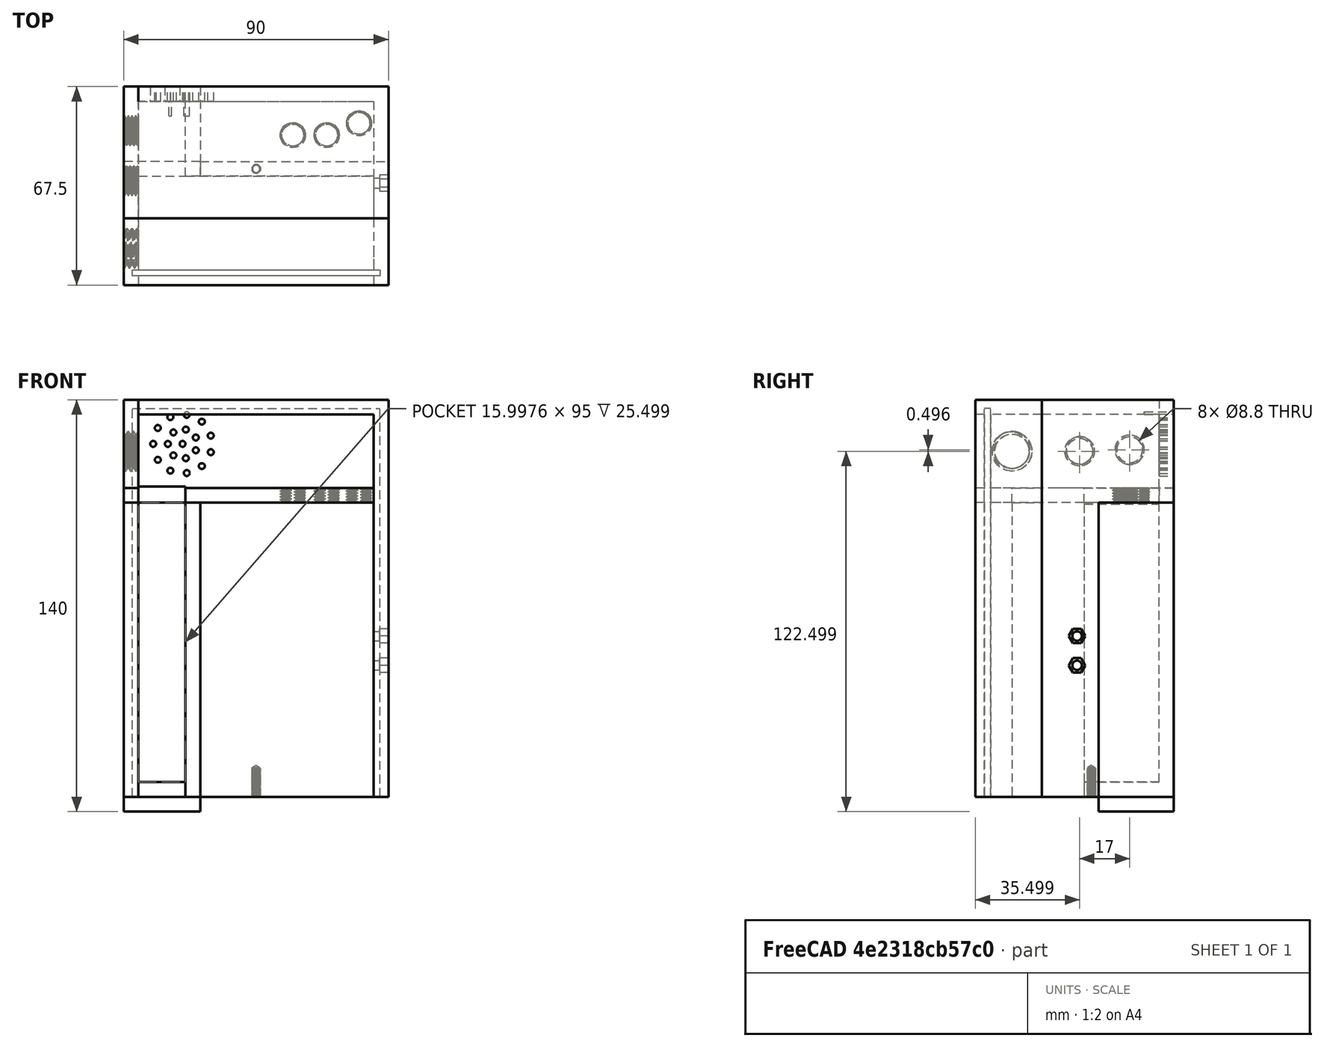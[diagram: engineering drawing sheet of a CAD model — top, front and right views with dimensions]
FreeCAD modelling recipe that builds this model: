
FCSTD DOCUMENT  (FreeCAD 1.0R39285 (Git))
Label: QMX_batterycase7b
License: All rights reserved
LicenseURL: https://en.wikipedia.org/wiki/All_rights_reserved
objects: Sketcher::SketchObject×24, PartDesign::Pad×22, PartDesign::Pocket×10, PartDesign::Hole×5, Part::FeaturePython×3, PartDesign::PolarPattern×2, PartDesign::Body×2, Part::Extrusion×2, App::DocumentObjectGroup×1, PartDesign::FeatureBase×1
note: 172 computed .brp shape members not serialized (recipe doc carries the construction recipe); baked Part::Feature solids carry a one-line shape summary decoded from their .brp

FEATURE [Sketcher::SketchObject] Sketch
  ArcFitTolerance = 1e-06
  FullyConstrained = true
  MakeInternals = false
  sketch-geometry (7):
    g0: LineSegment StartX=0 StartY=0 StartZ=0 EndX=0 EndY=25 EndZ=0
    g1: LineSegment StartX=0 StartY=25 StartZ=0 EndX=-45 EndY=25 EndZ=0
    g2: LineSegment StartX=-45 StartY=25 StartZ=0 EndX=-45 EndY=0 EndZ=0
    g3: LineSegment StartX=-45 StartY=0 StartZ=0 EndX=0 EndY=0 EndZ=0
    g4: Circle CenterX=-32.5 CenterY=8.5 CenterZ=0 NormalX=0 NormalY=0 NormalZ=1 AngleXU=0 Radius=3.65
    g5: Circle CenterX=-21 CenterY=8.5 CenterZ=0 NormalX=0 NormalY=0 NormalZ=1 AngleXU=0 Radius=3.7
    g6: Circle CenterX=-10 CenterY=12.5 CenterZ=0 NormalX=0 NormalY=0 NormalZ=1 AngleXU=0 Radius=3.75
  constraints (20):
    c: Coincident(g0,g1)
    c: Coincident(g1,g2)
    c: Coincident(g2,g3)
    c: Coincident(g3,g0)
    c: Vertical(g0)
    c: Vertical(g2)
    c: Horizontal(g1)
    c: Horizontal(g3)
    c: Distance(g0,g2) = 45
    c: Distance(g1,g3) = 25
    c: Coincident(g0,g-1)
    c: Diameter(g4) = 7.3
    c: Diameter(g5) = 7.4
    c: Diameter(g6) = 7.5
    c: DistanceX(g4) = -32.5
    c: DistanceY(g4) = 8.5
    c: DistanceX(g5) = -21
    c: DistanceY(g5) = 8.5
    c: DistanceX(g6) = -10
    c: DistanceY(g6) = 12.5
FEATURE [PartDesign::Pad] Pad
  Direction = (0,0,1)
  Length = 5
  Length2 = 10
  Profile = -> Sketch
  ReferenceAxis = -> Sketch [N_Axis]
  Refine = true
  Suppressed = false
  Type = 0
FEATURE [PartDesign::Hole] Hole
  BaseFeature = -> Pad
  CustomThreadClearance = 1.5
  Depth = 25
  DepthType = 0
  Diameter = 7.5
  DrillForDepth = false
  DrillPoint = 1
  DrillPointAngle = 118
  HoleCutCountersinkAngle = 90
  HoleCutCustomValues = false
  HoleCutDepth = 0
  HoleCutDiameter = 7.1
  HoleCutType = 0
  ModelThread = true
  Profile = -> Pad [Edge21,Edge18,Edge15]
  Refine = true
  Suppressed = false
  Tapered = false
  TaperedAngle = 90
  ThreadClass = 0
  ThreadDepth = 25
  ThreadDepthType = 0
  ThreadDirection = 0
  ThreadFit = 0
  ThreadSize = 15
  ThreadType = 1
  Threaded = true
  UseCustomThreadClearance = true
FEATURE [PartDesign::Pad] Pad001
  BaseFeature = -> Hole
  Direction = (-1,0,0)
  Length = 18
  Length2 = 10
  Profile = -> Hole [Face6]
  Refine = true
  Suppressed = false
  Type = 0
FEATURE [PartDesign::Pad] Pad002
  BaseFeature = -> Pad001
  Direction = (0,-1,0)
  Length = 25
  Length2 = 10
  Profile = -> Pad001 [Face2]
  Refine = true
  Suppressed = false
  Type = 0
FEATURE [Sketcher::SketchObject] Sketch001
  ArcFitTolerance = 1e-06
  AttachmentSupport = -> [Pad002]
  FullyConstrained = true
  MakeInternals = false
  MapMode = 5
  Placement = pos=(0,0,5) rot=(0,0,1;0rad)
FEATURE [PartDesign::Pad] Pad003
  BaseFeature = -> Pad002
  Direction = (-1,0,0)
  Length = 27
  Length2 = 10
  Profile = -> Pad002 [Face75]
  Refine = true
  Suppressed = false
  Type = 0
FEATURE [Sketcher::SketchObject] Sketch002
  ArcFitTolerance = 1e-06
  AttachmentSupport = -> [Pad003]
  FullyConstrained = false
  MakeInternals = false
  MapMode = 5
  Placement = pos=(0,0,5) rot=(0,0,1;0rad)
  sketch-geometry (4):
    g0: LineSegment StartX=-5 StartY=25 StartZ=0 EndX=-5 EndY=-25 EndZ=0
    g1: LineSegment StartX=-5 StartY=-25 StartZ=0 EndX=0 EndY=-25 EndZ=0
    g2: LineSegment StartX=0 StartY=-25 StartZ=0 EndX=0 EndY=25 EndZ=0
    g3: LineSegment StartX=0 StartY=25 StartZ=0 EndX=-5 EndY=25 EndZ=0
  constraints (11):
    c: Coincident(g0,g1)
    c: Coincident(g1,g2)
    c: Coincident(g2,g3)
    c: Coincident(g3,g0)
    c: Vertical(g0)
    c: Vertical(g2)
    c: Horizontal(g1)
    c: Horizontal(g3)
    c: Distance(g0,g2) = 5
    c: Distance(g1,g3) = 50
    c: PointOnObject(g1,g-2)
FEATURE [PartDesign::Pad] Pad004
  BaseFeature = -> Pad003
  Direction = (0,0,1)
  Length = 30
  Length2 = 10
  Profile = -> Sketch002
  ReferenceAxis = -> Sketch002 [N_Axis]
  Refine = true
  Suppressed = false
  Type = 0
FEATURE [Sketcher::SketchObject] Sketch003
  ArcFitTolerance = 1e-06
  AttachmentSupport = -> [Pad004]
  FullyConstrained = false
  MakeInternals = false
  MapMode = 5
  Placement = pos=(0,0,5) rot=(0,0,1;0rad)
  sketch-geometry (4):
    g0: LineSegment StartX=-90 StartY=25.0006 StartZ=0 EndX=-90 EndY=-24.9994 EndZ=0
    g1: LineSegment StartX=-90 StartY=-24.9994 StartZ=0 EndX=-85 EndY=-24.9994 EndZ=0
    g2: LineSegment StartX=-85 StartY=-24.9994 StartZ=0 EndX=-85 EndY=25.0006 EndZ=0
    g3: LineSegment StartX=-85 StartY=25.0006 StartZ=0 EndX=-90 EndY=25.0006 EndZ=0
  constraints (10):
    c: Coincident(g0,g1)
    c: Coincident(g1,g2)
    c: Coincident(g2,g3)
    c: Coincident(g3,g0)
    c: Vertical(g0)
    c: Vertical(g2)
    c: Horizontal(g1)
    c: Horizontal(g3)
    c: Distance(g0,g2) = 5
    c: Distance(g1,g3) = 50
FEATURE [PartDesign::Pad] Pad005
  BaseFeature = -> Pad004
  Direction = (0,0,1)
  Length = 30
  Length2 = 10
  Profile = -> Sketch003
  ReferenceAxis = -> Sketch003 [N_Axis]
  Refine = true
  Suppressed = false
  Type = 0
FEATURE [Sketcher::SketchObject] Sketch004
  ArcFitTolerance = 1e-06
  AttachmentSupport = -> [Pad005]
  FullyConstrained = false
  MakeInternals = false
  MapMode = 5
  Placement = pos=(0,0,5) rot=(0,0,1;0rad)
  sketch-geometry (4):
    g0: LineSegment StartX=-84.9972 StartY=24.9988 StartZ=0 EndX=-84.9972 EndY=19.9988 EndZ=0
    g1: LineSegment StartX=-84.9972 StartY=19.9988 StartZ=0 EndX=-4.99721 EndY=19.9988 EndZ=0
    g2: LineSegment StartX=-4.99721 StartY=19.9988 StartZ=0 EndX=-4.99721 EndY=24.9988 EndZ=0
    g3: LineSegment StartX=-4.99721 StartY=24.9988 StartZ=0 EndX=-84.9972 EndY=24.9988 EndZ=0
  constraints (10):
    c: Coincident(g0,g1)
    c: Coincident(g1,g2)
    c: Coincident(g2,g3)
    c: Coincident(g3,g0)
    c: Vertical(g0)
    c: Vertical(g2)
    c: Horizontal(g1)
    c: Horizontal(g3)
    c: Distance(g0,g2) = 80
    c: Distance(g1,g3) = 5
FEATURE [PartDesign::Pad] Pad006
  BaseFeature = -> Pad005
  Direction = (0,0,1)
  Length = 30
  Length2 = 10
  Profile = -> Sketch004
  ReferenceAxis = -> Sketch004 [N_Axis]
  Refine = true
  Suppressed = false
  Type = 0
FEATURE [Sketcher::SketchObject] Sketch005
  ArcFitTolerance = 1e-06
  AttachmentSupport = -> [Pad006]
  FullyConstrained = false
  MakeInternals = false
  MapMode = 5
  Placement = pos=(-5,0,0) rot=(0.57735,-0.57735,-0.57735;2.0944rad)
  sketch-geometry (4):
    g0: LineSegment StartX=-20 StartY=35 StartZ=0 EndX=-20 EndY=30 EndZ=0
    g1: LineSegment StartX=-20 StartY=30 StartZ=0 EndX=25 EndY=30 EndZ=0
    g2: LineSegment StartX=25 StartY=30 StartZ=0 EndX=25 EndY=35 EndZ=0
    g3: LineSegment StartX=25 StartY=35 StartZ=0 EndX=-20 EndY=35 EndZ=0
  constraints (10):
    c: Coincident(g0,g1)
    c: Coincident(g1,g2)
    c: Coincident(g2,g3)
    c: Coincident(g3,g0)
    c: Vertical(g0)
    c: Vertical(g2)
    c: Horizontal(g1)
    c: Horizontal(g3)
    c: Distance(g0,g2) = 45
    c: Distance(g1,g3) = 5
FEATURE [PartDesign::Pad] Pad007
  BaseFeature = -> Pad006
  Direction = (-1,0,0)
  Length = 80
  Length2 = 10
  Profile = -> Sketch005
  ReferenceAxis = -> Sketch005 [N_Axis]
  Refine = true
  Suppressed = false
  Type = 0
FEATURE [Sketcher::SketchObject] Sketch006
  ArcFitTolerance = 1e-06
  AttachmentSupport = -> [Pad007]
  FullyConstrained = false
  MakeInternals = false
  MapMode = 5
  Placement = pos=(0,0,0) rot=(1,0,0;3.14159rad)
  sketch-geometry (4):
    g0: LineSegment StartX=-90 StartY=25.0014 StartZ=0 EndX=-90 EndY=-24.9986 EndZ=0
    g1: LineSegment StartX=-90 StartY=-24.9986 StartZ=0 EndX=-85 EndY=-24.9986 EndZ=0
    g2: LineSegment StartX=-85 StartY=-24.9986 StartZ=0 EndX=-85 EndY=25.0014 EndZ=0
    g3: LineSegment StartX=-85 StartY=25.0014 StartZ=0 EndX=-90 EndY=25.0014 EndZ=0
  constraints (10):
    c: Coincident(g0,g1)
    c: Coincident(g1,g2)
    c: Coincident(g2,g3)
    c: Coincident(g3,g0)
    c: Vertical(g0)
    c: Vertical(g2)
    c: Horizontal(g1)
    c: Horizontal(g3)
    c: Distance(g0,g2) = 5
    c: Distance(g1,g3) = 50
FEATURE [PartDesign::Pad] Pad008
  BaseFeature = -> Pad007
  Direction = (0,0,-1)
  Length = 100
  Length2 = 10
  Profile = -> Sketch006
  ReferenceAxis = -> Sketch006 [N_Axis]
  Refine = true
  Suppressed = false
  Type = 0
FEATURE [Sketcher::SketchObject] Sketch007
  ArcFitTolerance = 1e-06
  AttachmentSupport = -> [Pad008]
  FullyConstrained = true
  MakeInternals = false
  MapMode = 5
  Placement = pos=(0,0,0) rot=(1,0,0;3.14159rad)
  sketch-geometry (4):
    g0: LineSegment StartX=0 StartY=0.5 StartZ=0 EndX=0 EndY=5.5 EndZ=0
    g1: LineSegment StartX=0 StartY=5.5 StartZ=0 EndX=-64 EndY=5.5 EndZ=0
    g2: LineSegment StartX=-64 StartY=5.5 StartZ=0 EndX=-64 EndY=0.5 EndZ=0
    g3: LineSegment StartX=-64 StartY=0.5 StartZ=0 EndX=0 EndY=0.5 EndZ=0
  constraints (11):
    c: Coincident(g0,g1)
    c: Coincident(g1,g2)
    c: Coincident(g2,g3)
    c: Coincident(g3,g0)
    c: Vertical(g0)
    c: Vertical(g2)
    c: Horizontal(g1)
    c: Horizontal(g3)
    c: Distance(g0,g2) = 64
    c: Distance(g1,g3) = 5
    c: Symmetric(g-2,g-2,g0)
FEATURE [PartDesign::Pad] Pad009
  BaseFeature = -> Pad008
  Direction = (0,0,-1)
  Length = 100
  Length2 = 10
  Profile = -> Sketch007
  ReferenceAxis = -> Sketch007 [N_Axis]
  Refine = true
  Suppressed = false
  Type = 0
FEATURE [PartDesign::Pad] Pad010
  BaseFeature = -> Pad009
  Direction = (0,-1,0)
  Length = 12.5
  Length2 = 10
  Profile = -> Pad009 [Face2]
  Refine = true
  Suppressed = false
  Type = 0
FEATURE [PartDesign::Pad] Pad011
  BaseFeature = -> Pad010
  Direction = (0,-1,0)
  Length = 12.5
  Length2 = 10
  Profile = -> Pad010 [Face52]
  Refine = true
  Suppressed = false
  Type = 0
FEATURE [PartDesign::Pad] Pad012
  BaseFeature = -> Pad011
  Direction = (0,-1,0)
  Length = 12.5
  Length2 = 10
  Profile = -> Pad011 [Face16]
  Refine = true
  Suppressed = false
  Type = 0
FEATURE [PartDesign::Pad] Pad013
  BaseFeature = -> Pad012
  Direction = (0,-1,0)
  Length = 12.5
  Length2 = 10
  Profile = -> Pad012 [Face38]
  Refine = true
  Suppressed = false
  Type = 0
FEATURE [Sketcher::SketchObject] Sketch008
  ArcFitTolerance = 1e-06
  AttachmentSupport = -> [Pad013]
  FullyConstrained = true
  MakeInternals = false
  MapMode = 5
  Placement = pos=(0,-25,0) rot=(1,0,0;1.5708rad)
  sketch-geometry (4):
    g0: LineSegment StartX=0 StartY=0 StartZ=0 EndX=0 EndY=5 EndZ=0
    g1: LineSegment StartX=0 StartY=5 StartZ=0 EndX=-5 EndY=5 EndZ=0
    g2: LineSegment StartX=-5 StartY=5 StartZ=0 EndX=-5 EndY=0 EndZ=0
    g3: LineSegment StartX=-5 StartY=0 StartZ=0 EndX=0 EndY=0 EndZ=0
  constraints (11):
    c: Coincident(g0,g1)
    c: Coincident(g1,g2)
    c: Coincident(g2,g3)
    c: Coincident(g3,g0)
    c: Vertical(g0)
    c: Vertical(g2)
    c: Horizontal(g1)
    c: Horizontal(g3)
    c: Distance(g0,g2) = 5
    c: Distance(g1,g3) = 5
    c: Coincident(g0,g-1)
FEATURE [PartDesign::Pad] Pad014
  BaseFeature = -> Pad013
  Direction = (0,-1,2e-16)
  Length = 12.5
  Length2 = 10
  Profile = -> Sketch008
  ReferenceAxis = -> Sketch008 [N_Axis]
  Refine = true
  Suppressed = false
  Type = 0
FEATURE [Sketcher::SketchObject] Sketch009
  ArcFitTolerance = 1e-06
  AttachmentSupport = -> [Pad014]
  FullyConstrained = false
  MakeInternals = false
  MapMode = 5
  Placement = pos=(0,-25,0) rot=(1,0,0;1.5708rad)
  sketch-geometry (4):
    g0: LineSegment StartX=-90.0021 StartY=0 StartZ=0 EndX=-85.0021 EndY=0 EndZ=0
    g1: LineSegment StartX=-85.0021 StartY=0 StartZ=0 EndX=-85.0021 EndY=5 EndZ=0
    g2: LineSegment StartX=-85.0021 StartY=5 StartZ=0 EndX=-90.0021 EndY=5 EndZ=0
    g3: LineSegment StartX=-90.0021 StartY=5 StartZ=0 EndX=-90.0021 EndY=0 EndZ=0
  constraints (11):
    c: Coincident(g0,g1)
    c: Coincident(g1,g2)
    c: Coincident(g2,g3)
    c: Coincident(g3,g0)
    c: Horizontal(g0)
    c: Horizontal(g2)
    c: Vertical(g1)
    c: Vertical(g3)
    c: Distance(g1,g3) = 5
    c: Distance(g0,g2) = 5
    c: PointOnObject(g0,g-1)
FEATURE [PartDesign::Pad] Pad015
  BaseFeature = -> Pad014
  Direction = (0,-1,2e-16)
  Length = 12.5
  Length2 = 10
  Profile = -> Sketch009
  ReferenceAxis = -> Sketch009 [N_Axis]
  Refine = true
  Suppressed = false
  Type = 0
FEATURE [Sketcher::SketchObject] Sketch010
  ArcFitTolerance = 1e-06
  AttachmentSupport = -> [Pad015]
  FullyConstrained = false
  MakeInternals = false
  MapMode = 5
  Placement = pos=(0,0,1e-16) rot=(1,0,0;3.14159rad)
  sketch-geometry (4):
    g0: LineSegment StartX=-5.0009 StartY=5.50037 StartZ=0 EndX=-5.0009 EndY=25.0004 EndZ=0
    g1: LineSegment StartX=-5.0009 StartY=25.0004 StartZ=0 EndX=-85.0009 EndY=25.0004 EndZ=0
    g2: LineSegment StartX=-85.0009 StartY=25.0004 StartZ=0 EndX=-85.0009 EndY=5.50037 EndZ=0
    g3: LineSegment StartX=-85.0009 StartY=5.50037 StartZ=0 EndX=-5.0009 EndY=5.50037 EndZ=0
  constraints (10):
    c: Coincident(g0,g1)
    c: Coincident(g1,g2)
    c: Coincident(g2,g3)
    c: Coincident(g3,g0)
    c: Vertical(g0)
    c: Vertical(g2)
    c: Horizontal(g1)
    c: Horizontal(g3)
    c: Distance(g0,g2) = 80
    c: Distance(g1,g3) = 19.5
FEATURE [PartDesign::Pocket] Pocket
  BaseFeature = -> Pad015
  Direction = (0,0,1)
  Length = 5
  Length2 = 5
  Profile = -> Sketch010
  ReferenceAxis = -> Sketch010 [N_Axis]
  Refine = true
  Suppressed = false
  Type = 0
FEATURE [PartDesign::Pad] Pad016
  BaseFeature = -> Pocket
  Direction = (0,0,-1)
  Length = 100
  Length2 = 10
  Profile = -> Pocket [Face43]
  Refine = true
  Suppressed = false
  Type = 0
FEATURE [Sketcher::SketchObject] Sketch011
  ArcFitTolerance = 1e-06
  AttachmentSupport = -> [Pad016]
  FullyConstrained = false
  MakeInternals = false
  MapMode = 5
  Placement = pos=(0,0,1e-16) rot=(1,0,0;3.14159rad)
  sketch-geometry (4):
    g0: LineSegment StartX=-64.0024 StartY=5.49883 StartZ=0 EndX=-69.0024 EndY=5.49883 EndZ=0
    g1: LineSegment StartX=-69.0024 StartY=5.49883 StartZ=0 EndX=-69.0024 EndY=-25.0012 EndZ=0
    g2: LineSegment StartX=-69.0024 StartY=-25.0012 StartZ=0 EndX=-64.0024 EndY=-25.0012 EndZ=0
    g3: LineSegment StartX=-64.0024 StartY=-25.0012 StartZ=0 EndX=-64.0024 EndY=5.49883 EndZ=0
  constraints (10):
    c: Coincident(g0,g1)
    c: Coincident(g1,g2)
    c: Coincident(g2,g3)
    c: Coincident(g3,g0)
    c: Horizontal(g0)
    c: Horizontal(g2)
    c: Vertical(g1)
    c: Vertical(g3)
    c: Distance(g1,g3) = 5
    c: Distance(g0,g2) = 30.5
FEATURE [PartDesign::Pad] Pad017
  BaseFeature = -> Pad016
  Direction = (0,0,-1)
  Length = 100
  Length2 = 10
  Profile = -> Sketch011
  ReferenceAxis = -> Sketch011 [N_Axis]
  Refine = true
  Suppressed = false
  Type = 0
FEATURE [Sketcher::SketchObject] Sketch012
  ArcFitTolerance = 1e-06
  AttachmentSupport = -> [Pad017]
  FullyConstrained = false
  MakeInternals = false
  MapMode = 5
  Placement = pos=(0,0,1e-16) rot=(1,0,0;3.14159rad)
  sketch-geometry (4):
    g0: LineSegment StartX=-85.1641 StartY=-20 StartZ=0 EndX=-85.1641 EndY=-25 EndZ=0
    g1: LineSegment StartX=-85.1641 StartY=-25 StartZ=0 EndX=-68.6641 EndY=-25 EndZ=0
    g2: LineSegment StartX=-68.6641 StartY=-25 StartZ=0 EndX=-68.6641 EndY=-20 EndZ=0
    g3: LineSegment StartX=-68.6641 StartY=-20 StartZ=0 EndX=-85.1641 EndY=-20 EndZ=0
  constraints (10):
    c: Coincident(g0,g1)
    c: Coincident(g1,g2)
    c: Coincident(g2,g3)
    c: Coincident(g3,g0)
    c: Vertical(g0)
    c: Vertical(g2)
    c: Horizontal(g1)
    c: Horizontal(g3)
    c: Distance(g0,g2) = 16.5
    c: Distance(g1,g3) = 5
FEATURE [PartDesign::Pad] Pad018
  BaseFeature = -> Pad017
  Direction = (0,0,-1)
  Length = 100
  Length2 = 10
  Profile = -> Sketch012
  ReferenceAxis = -> Sketch012 [N_Axis]
  Refine = true
  Suppressed = false
  Type = 0
FEATURE [Sketcher::SketchObject] Sketch013
  ArcFitTolerance = 1e-06
  AttachmentSupport = -> [Pad018]
  FullyConstrained = false
  MakeInternals = false
  MapMode = 5
  Placement = pos=(-85,0,0) rot=(0.57735,0.57735,0.57735;2.0944rad)
  sketch-geometry (4):
    g0: LineSegment StartX=20 StartY=-100 StartZ=0 EndX=20 EndY=-95 EndZ=0
    g1: LineSegment StartX=20 StartY=-95 StartZ=0 EndX=-5.5 EndY=-95 EndZ=0
    g2: LineSegment StartX=-5.5 StartY=-95 StartZ=0 EndX=-5.5 EndY=-100 EndZ=0
    g3: LineSegment StartX=-5.5 StartY=-100 StartZ=0 EndX=20 EndY=-100 EndZ=0
  constraints (10):
    c: Coincident(g0,g1)
    c: Coincident(g1,g2)
    c: Coincident(g2,g3)
    c: Coincident(g3,g0)
    c: Vertical(g0)
    c: Vertical(g2)
    c: Horizontal(g1)
    c: Horizontal(g3)
    c: Distance(g0,g2) = 25.5
    c: Distance(g1,g3) = 5
FEATURE [PartDesign::Pad] Pad019
  BaseFeature = -> Pad018
  Direction = (1,0,0)
  Length = 16
  Length2 = 10
  Profile = -> Sketch013
  ReferenceAxis = -> Sketch013 [N_Axis]
  Refine = true
  Suppressed = false
  Type = 0
FEATURE [Sketcher::SketchObject] Sketch014
  ArcFitTolerance = 1e-06
  AttachmentSupport = -> [Pad019]
  FullyConstrained = false
  MakeInternals = false
  MapMode = 5
  Placement = pos=(0,-5.50037,0) rot=(1,0,0;1.5708rad)
  sketch-geometry (4):
    g0: LineSegment StartX=-84.9964 StartY=5.49791 StartZ=0 EndX=-84.9964 EndY=-0.50209 EndZ=0
    g1: LineSegment StartX=-84.9964 StartY=-0.50209 StartZ=0 EndX=-68.9964 EndY=-0.50209 EndZ=0
    g2: LineSegment StartX=-68.9964 StartY=-0.50209 StartZ=0 EndX=-68.9964 EndY=5.49791 EndZ=0
    g3: LineSegment StartX=-68.9964 StartY=5.49791 StartZ=0 EndX=-84.9964 EndY=5.49791 EndZ=0
  constraints (10):
    c: Coincident(g0,g1)
    c: Coincident(g1,g2)
    c: Coincident(g2,g3)
    c: Coincident(g3,g0)
    c: Vertical(g0)
    c: Vertical(g2)
    c: Horizontal(g1)
    c: Horizontal(g3)
    c: Distance(g0,g2) = 16
    c: Distance(g1,g3) = 6
FEATURE [PartDesign::Pocket] Pocket001
  BaseFeature = -> Pad019
  Direction = (0,1,-2e-16)
  Length = 25.5
  Length2 = 5
  Profile = -> Sketch014
  ReferenceAxis = -> Sketch014 [N_Axis]
  Refine = true
  Suppressed = false
  Type = 0
FEATURE [Sketcher::SketchObject] Sketch015
  ArcFitTolerance = 1e-06
  AttachmentSupport = -> [Pocket001]
  FullyConstrained = false
  MakeInternals = false
  MapMode = 5
  Placement = pos=(0,0,-100) rot=(1,0,0;3.14159rad)
  sketch-geometry (4):
    g0: LineSegment StartX=-2.90413 StartY=34.399 StartZ=0 EndX=-87.1041 EndY=34.399 EndZ=0
    g1: LineSegment StartX=-87.1041 StartY=34.399 StartZ=0 EndX=-87.1041 EndY=32.299 EndZ=0
    g2: LineSegment StartX=-87.1041 StartY=32.299 StartZ=0 EndX=-2.90413 EndY=32.299 EndZ=0
    g3: LineSegment StartX=-2.90413 StartY=32.299 StartZ=0 EndX=-2.90413 EndY=34.399 EndZ=0
  constraints (10):
    c: Coincident(g0,g1)
    c: Coincident(g1,g2)
    c: Coincident(g2,g3)
    c: Coincident(g3,g0)
    c: Horizontal(g0)
    c: Horizontal(g2)
    c: Vertical(g1)
    c: Vertical(g3)
    c: Distance(g1,g3) = 84.2
    c: Distance(g0,g2) = 2.1
FEATURE [PartDesign::Pocket] Pocket002
  BaseFeature = -> Pocket001
  Direction = (0,0,1)
  Length = 132.1
  Length2 = 5
  Profile = -> Sketch015
  ReferenceAxis = -> Sketch015 [N_Axis]
  Refine = true
  Suppressed = false
  Type = 0
FEATURE [Sketcher::SketchObject] Sketch016
  ArcFitTolerance = 1e-06
  AttachmentSupport = -> [Pocket002]
  FullyConstrained = false
  MakeInternals = false
  MapMode = 5
  Placement = pos=(0,0,-100) rot=(1,0,0;3.14159rad)
  sketch-geometry (4):
    g0: LineSegment StartX=-90 StartY=-24.9973 StartZ=0 EndX=-64 EndY=-24.9973 EndZ=0
    g1: LineSegment StartX=-64 StartY=-24.9973 StartZ=0 EndX=-64 EndY=0.502741 EndZ=0
    g2: LineSegment StartX=-64 StartY=0.502741 StartZ=0 EndX=-90 EndY=0.502741 EndZ=0
    g3: LineSegment StartX=-90 StartY=0.502741 StartZ=0 EndX=-90 EndY=-24.9973 EndZ=0
  constraints (10):
    c: Coincident(g0,g1)
    c: Coincident(g1,g2)
    c: Coincident(g2,g3)
    c: Coincident(g3,g0)
    c: Horizontal(g0)
    c: Horizontal(g2)
    c: Vertical(g1)
    c: Vertical(g3)
    c: Distance(g1,g3) = 26
    c: Distance(g0,g2) = 25.5
FEATURE [PartDesign::Pad] Pad020
  BaseFeature = -> Pocket002
  Direction = (0,0,-1)
  Length = 5
  Length2 = 10
  Profile = -> Sketch016
  ReferenceAxis = -> Sketch016 [N_Axis]
  Refine = true
  Suppressed = false
  Type = 0
FEATURE [Sketcher::SketchObject] Sketch017
  ArcFitTolerance = 1e-06
  AttachmentSupport = -> [Pad020]
  FullyConstrained = false
  MakeInternals = false
  MapMode = 5
  Placement = pos=(-85,0,0) rot=(0.57735,0.57735,0.57735;2.0944rad)
  sketch-geometry (1):
    g0: Circle CenterX=-24.9959 CenterY=17.5004 CenterZ=0 NormalX=0 NormalY=0 NormalZ=1 AngleXU=0 Radius=5.5
  constraints (1):
    c: Diameter(g0) = 11
FEATURE [PartDesign::Pocket] Pocket003
  BaseFeature = -> Pad020
  Direction = (-1,0,0)
  Length = 5
  Length2 = 5
  Profile = -> Sketch017
  ReferenceAxis = -> Sketch017 [N_Axis]
  Refine = true
  Suppressed = false
  Type = 0
FEATURE [PartDesign::Hole] Hole001
  BaseFeature = -> Pocket003
  CustomThreadClearance = 1.5
  Depth = 25
  DepthType = 0
  Diameter = 11.7
  DrillForDepth = false
  DrillPoint = 1
  DrillPointAngle = 118
  HoleCutCountersinkAngle = 90
  HoleCutCustomValues = false
  HoleCutDepth = 0
  HoleCutDiameter = 6.1
  HoleCutType = 0
  ModelThread = true
  Profile = -> Sketch017
  Refine = true
  Suppressed = false
  Tapered = false
  TaperedAngle = 90
  ThreadClass = 0
  ThreadDepth = 25
  ThreadDepthType = 0
  ThreadDirection = 0
  ThreadFit = 0
  ThreadSize = 20
  ThreadType = 1
  Threaded = true
  UseCustomThreadClearance = true
FEATURE [Sketcher::SketchObject] Sketch018
  ArcFitTolerance = 1e-06
  AttachmentSupport = -> [Hole001]
  FullyConstrained = false
  MakeInternals = false
  MapMode = 5
  Placement = pos=(-85,0,0) rot=(0.57735,0.57735,0.57735;2.0944rad)
  sketch-geometry (1):
    g0: Circle CenterX=-7.00046 CenterY=17.4988 CenterZ=0 NormalX=0 NormalY=0 NormalZ=1 AngleXU=0 Radius=4.5
  constraints (1):
    c: Diameter(g0) = 9
FEATURE [PartDesign::Hole] Hole002
  BaseFeature = -> Hole001
  CustomThreadClearance = 2
  Depth = 25
  DepthType = 0
  Diameter = 8.8
  DrillForDepth = false
  DrillPoint = 1
  DrillPointAngle = 118
  HoleCutCountersinkAngle = 90
  HoleCutCustomValues = false
  HoleCutDepth = 0
  HoleCutDiameter = 6.1
  HoleCutType = 0
  ModelThread = true
  Profile = -> Sketch018
  Refine = true
  Suppressed = false
  Tapered = false
  TaperedAngle = 90
  ThreadClass = 0
  ThreadDepth = 25
  ThreadDepthType = 0
  ThreadDirection = 0
  ThreadFit = 0
  ThreadSize = 16
  ThreadType = 1
  Threaded = true
  UseCustomThreadClearance = true
FEATURE [Sketcher::SketchObject] Sketch019
  ArcFitTolerance = 1e-06
  AttachmentSupport = -> [Hole002]
  FullyConstrained = false
  MakeInternals = false
  MapMode = 5
  Placement = pos=(0,24.9988,0) rot=(0,0.707107,0.707107;3.14159rad)
  sketch-geometry (4):
    g0: Circle CenterX=70 CenterY=20 CenterZ=0 NormalX=0 NormalY=0 NormalZ=1 AngleXU=0 Radius=12.5
    g1: Circle CenterX=80 CenterY=20 CenterZ=0 NormalX=0 NormalY=0 NormalZ=1 AngleXU=0 Radius=1
    g2: Circle CenterX=70 CenterY=20 CenterZ=0 NormalX=0 NormalY=0 NormalZ=1 AngleXU=0 Radius=1
    g3: Circle CenterX=74.9999 CenterY=20 CenterZ=0 NormalX=0 NormalY=0 NormalZ=1 AngleXU=0 Radius=1
  constraints (5):
    c: Diameter(g0) = 25
    c: Diameter(g1) = 2
    c: Diameter(g2) = 2
    c: Coincident(g2,g0)
    c: Diameter(g3) = 2
FEATURE [PartDesign::Pocket] Pocket004
  BaseFeature = -> Hole002
  Direction = (0,-1,2e-16)
  Length = 10
  Length2 = 5
  Profile = -> Sketch019 [Edge2]
  ReferenceAxis = -> Sketch019 [N_Axis]
  Refine = true
  Suppressed = false
  Type = 0
FEATURE [PartDesign::Pocket] Pocket005
  BaseFeature = -> Pocket004
  Direction = (0,-1,2e-16)
  Length = 5
  Length2 = 5
  Profile = -> Sketch019 [Edge3]
  ReferenceAxis = -> Sketch019 [N_Axis]
  Refine = true
  Suppressed = false
  Type = 1
FEATURE [PartDesign::PolarPattern] PolarPattern
  Angle = 360
  Axis = -> Pocket005 [Edge365]
  BaseFeature = -> Pocket005
  Mode = 0
  Occurrences = 11
  Offset = 120
  Originals = -> [Pocket004]
  Refine = true
  Suppressed = false
  TransformMode = 0
FEATURE [PartDesign::Pocket] Pocket006
  BaseFeature = -> PolarPattern
  Direction = (0,-1,2e-16)
  Length = 5
  Length2 = 5
  Profile = -> Sketch019 [Edge4]
  ReferenceAxis = -> Sketch019 [N_Axis]
  Refine = true
  Suppressed = false
  Type = 1
FEATURE [PartDesign::PolarPattern] PolarPattern001
  Angle = 360
  Axis = -> Pocket006 [Edge384]
  BaseFeature = -> Pocket006
  Mode = 0
  Occurrences = 7
  Offset = 120
  Originals = -> [Pocket006]
  Refine = true
  Suppressed = false
  TransformMode = 0
FEATURE [Sketcher::SketchObject] Sketch020
  ArcFitTolerance = 1e-06
  AttachmentSupport = -> [PolarPattern001]
  FullyConstrained = false
  MakeInternals = false
  MapMode = 5
  Placement = pos=(-90,0,0) rot=(0.57735,-0.57735,-0.57735;2.0944rad)
  sketch-geometry (1):
    g0: LineSegment StartX=14.855 StartY=40.0003 StartZ=0 EndX=14.855 EndY=-110 EndZ=0
  constraints (2):
    c: Distance(g0) = 150
    c: Vertical(g0)
FEATURE [PartDesign::Body] Body
  AllowCompound = false
  Group = -> [Sketch,Pad,Hole,Pad001,Pad002,Pad003,Sketch002,Pad004,Sketch003,Pad005,Sketch004,Pad006,Sketch005,Pad007,Sketch006,Pad008,Sketch007,Pad009,Pad010,Pad011,Pad012,Pad013,Sketch008,Pad014,Sketch009,Pad015,Sketch010,Pocket,Pad016,Sketch011,Pad017,Sketch012,Pad018,Sketch013,Pad019,Sketch014,Pocket001,Sketch015,Pocket002,Sketch016,Pad020,Sketch017,Pocket003,Hole001,Sketch018,Sketch001,Hole002,Sketch019,+6 more]
  Origin = -> Origin
  Tip = -> PolarPattern001
FEATURE [Part::Extrusion] Extrude
  Base = -> Sketch020
  Dir = (1,0,0)
  DirMode = 0
  FaceMakerClass = Part::FaceMakerBullseye
  FaceMakerMode = 3
  LengthFwd = 150
  LengthRev = 0
  Solid = false
  Symmetric = false
FEATURE [Part::Extrusion] Extrude001
  Base = -> Sketch020
  Dir = (1,0,0)
  DirMode = 0
  FaceMakerClass = Part::FaceMakerBullseye
  FaceMakerMode = 3
  LengthFwd = 150
  LengthRev = 0
  Solid = false
  Symmetric = false
FEATURE [Part::FeaturePython] Slice  # WARN: FeaturePython — macro-defined, semantics opaque (R4)
  Base = -> Body
  Mode = 1
  Tolerance = 0
  Tools = -> [Extrude,Extrude001]
FEATURE [Part::FeaturePython] Slice_child0  label="Slice.0"  # WARN: FeaturePython — macro-defined, semantics opaque (R4)
  Base = -> Slice
  FilterType = 1
  Invert = false
  OverrideMaxVal = 0
  WindowFrom = 80
  WindowTo = 100
  items = 0
FEATURE [Part::FeaturePython] Slice_child1  label="Slice.1"  # WARN: FeaturePython — macro-defined, semantics opaque (R4)
  Base = -> Slice
  FilterType = 1
  Invert = false
  OverrideMaxVal = 0
  Placement = pos=(0,-5,0) rot=(0,0,1;0rad)
  WindowFrom = 80
  WindowTo = 100
  items = 1
FEATURE [App::DocumentObjectGroup] GrExplode_Slice  label="Exploded Slice"
  Group = -> [Slice_child0,Slice_child1]
FEATURE [PartDesign::FeatureBase] BaseFeature
  BaseFeature = -> Slice_child0
  Suppressed = false
FEATURE [PartDesign::Pad] Pad021
  BaseFeature = -> BaseFeature
  Direction = (0,-1,0)
  Length = 5
  Length2 = 10
  Profile = -> BaseFeature [Face52]
  Refine = true
  Suppressed = false
  Type = 0
FEATURE [Sketcher::SketchObject] Sketch021
  ArcFitTolerance = 1e-06
  AttachmentSupport = -> [Pad021]
  FullyConstrained = false
  MakeInternals = false
  MapMode = 5
  Placement = pos=(-90,-2.34e-14,0) rot=(0.57735,-0.57735,-0.57735;2.0944rad)
  sketch-geometry (1):
    g0: Circle CenterX=-10 CenterY=17.9952 CenterZ=0 NormalX=0 NormalY=0 NormalZ=1 AngleXU=0 Radius=4.5
  constraints (1):
    c: Diameter(g0) = 9
FEATURE [PartDesign::Hole] Hole003
  BaseFeature = -> Pad021
  CustomThreadClearance = 2
  Depth = 25
  DepthType = 0
  Diameter = 8.8
  DrillForDepth = false
  DrillPoint = 1
  DrillPointAngle = 118
  HoleCutCountersinkAngle = 90
  HoleCutCustomValues = false
  HoleCutDepth = 0
  HoleCutDiameter = 6.1
  HoleCutType = 0
  ModelThread = true
  Profile = -> Sketch021
  Refine = true
  Suppressed = false
  Tapered = false
  TaperedAngle = 90
  ThreadClass = 0
  ThreadDepth = 25
  ThreadDepthType = 0
  ThreadDirection = 0
  ThreadFit = 0
  ThreadSize = 16
  ThreadType = 1
  Threaded = true
  UseCustomThreadClearance = true
FEATURE [Sketcher::SketchObject] Sketch022
  ArcFitTolerance = 1e-06
  AttachmentSupport = -> [Hole003]
  FullyConstrained = false
  MakeInternals = false
  MapMode = 5
  Placement = pos=(0,0,-100) rot=(1,0,0;3.14159rad)
  sketch-geometry (1):
    g0: Circle CenterX=-44.9974 CenterY=3.00354 CenterZ=0 NormalX=0 NormalY=0 NormalZ=1 AngleXU=0 Radius=1.5
  constraints (1):
    c: Diameter(g0) = 3
FEATURE [PartDesign::Hole] Hole004
  BaseFeature = -> Hole003
  CustomThreadClearance = 0
  Depth = 10
  DepthType = 0
  Diameter = 2.5
  DrillForDepth = false
  DrillPoint = 1
  DrillPointAngle = 118
  HoleCutCountersinkAngle = 90
  HoleCutCustomValues = false
  HoleCutDepth = 0
  HoleCutDiameter = 6.1
  HoleCutType = 0
  ModelThread = true
  Profile = -> Sketch022 [Edge1]
  Suppressed = false
  Tapered = false
  TaperedAngle = 90
  ThreadClass = 0
  ThreadDepth = 10
  ThreadDepthType = 0
  ThreadDirection = 0
  ThreadFit = 0
  ThreadSize = 9
  ThreadType = 1
  Threaded = true
  UseCustomThreadClearance = true
FEATURE [Sketcher::SketchObject] Sketch023
  ArcFitTolerance = 1e-06
  AttachmentSupport = -> [Hole004]
  FullyConstrained = false
  MakeInternals = false
  MapMode = 5
  Placement = pos=(0,0,0) rot=(0.57735,0.57735,0.57735;2.0944rad)
  sketch-geometry (16):
    g0: LineSegment StartX=-5.06285 StartY=-45.3224 StartZ=0 EndX=-6.46285 EndY=-42.8976 EndZ=0
    g1: LineSegment StartX=-6.46285 StartY=-42.8976 StartZ=0 EndX=-9.26285 EndY=-42.8976 EndZ=0
    g2: LineSegment StartX=-9.26285 StartY=-42.8976 StartZ=0 EndX=-10.6629 EndY=-45.3224 EndZ=0
    g3: LineSegment StartX=-10.6629 StartY=-45.3224 StartZ=0 EndX=-9.26285 EndY=-47.7473 EndZ=0
    g4: LineSegment StartX=-9.26285 StartY=-47.7473 StartZ=0 EndX=-6.46285 EndY=-47.7473 EndZ=0
    g5: LineSegment StartX=-6.46285 StartY=-47.7473 StartZ=0 EndX=-5.06285 EndY=-45.3224 EndZ=0
    g6: Circle [constr] CenterX=-7.86285 CenterY=-45.3224 CenterZ=0 NormalX=0 NormalY=0 NormalZ=1 AngleXU=0 Radius=2.8
    g7: LineSegment StartX=-5.06376 StartY=-55.2691 StartZ=0 EndX=-6.46376 EndY=-52.8443 EndZ=0
    g8: LineSegment StartX=-6.46376 StartY=-52.8443 StartZ=0 EndX=-9.26376 EndY=-52.8443 EndZ=0
    g9: LineSegment StartX=-9.26376 StartY=-52.8443 StartZ=0 EndX=-10.6638 EndY=-55.2691 EndZ=0
    g10: LineSegment StartX=-10.6638 StartY=-55.2691 StartZ=0 EndX=-9.26376 EndY=-57.694 EndZ=0
    g11: LineSegment StartX=-9.26376 StartY=-57.694 StartZ=0 EndX=-6.46376 EndY=-57.694 EndZ=0
    g12: LineSegment StartX=-6.46376 StartY=-57.694 StartZ=0 EndX=-5.06376 EndY=-55.2691 EndZ=0
    g13: Circle [constr] CenterX=-7.86376 CenterY=-55.2691 CenterZ=0 NormalX=0 NormalY=0 NormalZ=1 AngleXU=0 Radius=2.8
    g14: Circle CenterX=-7.86285 CenterY=-45.3224 CenterZ=0 NormalX=0 NormalY=0 NormalZ=1 AngleXU=0 Radius=1.6
    g15: Circle CenterX=-7.86376 CenterY=-55.2691 CenterZ=0 NormalX=0 NormalY=0 NormalZ=1 AngleXU=0 Radius=1.6
  constraints (32):
    c: Coincident(g0,g1)
    c: Coincident(g1,g2)
    c: Coincident(g2,g3)
    c: Coincident(g3,g4)
    c: Coincident(g4,g5)
    c: Coincident(g5,g0)
    c: Equal(g0, g1-g5) x5
    c: PointOnObject(g0,g6)
    c: PointOnObject(g1,g6)
    c: PointOnObject(g2,g6)
    c: PointOnObject(g3,g6)
    c: PointOnObject(g4,g6)
    c: PointOnObject(g5,g6)
    c: Radius(g6) = 2.8
    c: Coincident(g7,g8)
    c: Coincident(g8,g9)
    c: Coincident(g9,g10)
    c: Coincident(g10,g11)
    c: Coincident(g11,g12)
    c: Coincident(g12,g7)
    c: Equal(g7, g8-g12) x5
    c: PointOnObject(g7,g13)
    c: PointOnObject(g8,g13)
    c: PointOnObject(g9,g13)
    c: PointOnObject(g10,g13)
    c: PointOnObject(g11,g13)
    c: PointOnObject(g12,g13)
    c: Radius(g13) = 2.8
    c: Diameter(g14) = 3.2
    c: Coincident(g14,g6)
    c: Diameter(g15) = 3.2
    c: Coincident(g15,g13)
FEATURE [PartDesign::Pocket] Pocket007
  BaseFeature = -> Hole004
  Direction = (-1,0,0)
  Length = 3
  Length2 = 5
  Profile = -> Sketch023
  ReferenceAxis = -> Sketch023 [N_Axis]
  Suppressed = false
  Type = 0
FEATURE [PartDesign::Pocket] Pocket008
  BaseFeature = -> Pocket007
  Direction = (-1,0,0)
  Length = 5
  Length2 = 5
  Profile = -> Pocket007 [Edge534]
  Suppressed = false
  Type = 0
FEATURE [PartDesign::Pocket] Pocket009
  BaseFeature = -> Pocket008
  Direction = (-1,0,0)
  Length = 5
  Length2 = 5
  Profile = -> Pocket008 [Edge536]
  Suppressed = false
  Type = 0
FEATURE [PartDesign::Body] Body001
  AllowCompound = false
  BaseFeature = -> Slice_child0
  Group = -> [BaseFeature,Pad021,Sketch021,Hole003,Sketch022,Hole004,Sketch023,Pocket007,Pocket008,Pocket009]
  Origin = -> Origin001
  Tip = -> Pocket009
